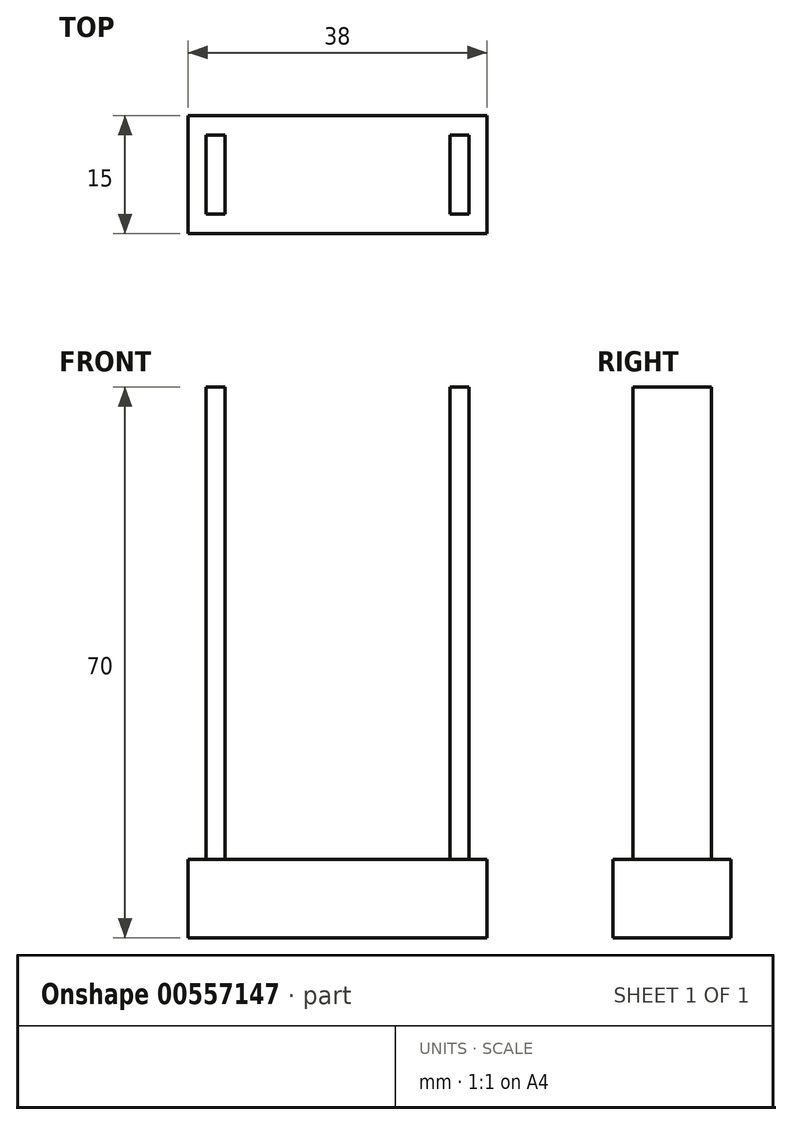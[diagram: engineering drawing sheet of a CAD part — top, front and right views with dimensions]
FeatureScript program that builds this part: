
annotation { "Feature Type Name" : "Feature", "Feature Type Description" : "" }
export const myFeature = defineFeature(function(context is Context, id is Id, definition is map)
    precondition{}
    {
        {
            var Q0;
            Q0=qCreatedBy(makeId("Top.planeOp"),FACE);
            var sketch = newSketch(context, id + "F0", { "sketchPlane" : qUnion([Q0])});
            skLineSegment(sketch, "E0", {"start": v(0, 0) * mm, "end": v(15.5, 0) * mm});
            skLineSegment(sketch, "E1", {"start": v(15.5, 0) * mm, "end": v(-15.5, 0) * mm});
            skLineSegment(sketch, "E2", {"start": v(-15.5, 0) * mm, "end": v(-14.3, 0) * mm});
            skLineSegment(sketch, "E3", {"start": v(-14.3, 0) * mm, "end": v(-14.3, 5) * mm});
            skLineSegment(sketch, "E4", {"start": v(-14.3, 5) * mm, "end": v(-14.3, -5) * mm});
            skLineSegment(sketch, "E5", {"start": v(-14.3, -5) * mm, "end": v(-16.7, -5) * mm});
            skLineSegment(sketch, "E6.bottom", {"start": v(-16.7, -5) * mm, "end": v(-14.3, -5) * mm});
            skLineSegment(sketch, "E6.top", {"start": v(-16.7, 5) * mm, "end": v(-14.3, 5) * mm});
            skLineSegment(sketch, "E6.left", {"start": v(-16.7, -5) * mm, "end": v(-16.7, 5) * mm});
            skLineSegment(sketch, "E6.right", {"start": v(-14.3, -5) * mm, "end": v(-14.3, 5) * mm});
            skLineSegment(sketch, "E7", {"start": v(15.5, 0) * mm, "end": v(14.3, 0) * mm});
            skLineSegment(sketch, "E8", {"start": v(14.3, 0) * mm, "end": v(14.3, 5) * mm});
            skLineSegment(sketch, "E9", {"start": v(14.3, 5) * mm, "end": v(14.3, -5) * mm});
            skLineSegment(sketch, "E10", {"start": v(14.3, -5) * mm, "end": v(16.7, -5) * mm});
            skLineSegment(sketch, "E11.bottom", {"start": v(14.3, 5) * mm, "end": v(16.7, 5) * mm});
            skLineSegment(sketch, "E11.right", {"start": v(16.7, 5) * mm, "end": v(16.7, -5) * mm});
            skSolve(sketch);
        }
        {
            var Q0;
            Q0=qCreatedBy(makeId("Top.planeOp"),FACE);
            var sketch = newSketch(context, id + "F1", { "sketchPlane" : qUnion([Q0])});
            skLineSegment(sketch, "E12.bottom", {"start": v(19, 7.5) * mm, "end": v(-19, 7.5) * mm});
            skLineSegment(sketch, "E12.top", {"start": v(19, -7.5) * mm, "end": v(-19, -7.5) * mm});
            skLineSegment(sketch, "E12.left", {"start": v(19, 7.5) * mm, "end": v(19, -7.5) * mm});
            skLineSegment(sketch, "E12.right", {"start": v(-19, 7.5) * mm, "end": v(-19, -7.5) * mm});
            skPoint(sketch, "E12.middle", {"position": v(0, 0) * mm});
            skSolve(sketch);
        }
        {
            var Q0;
            Q0 = qSketchRegion(id + "F0", true);
            extrude(context, id + "F2", {"entities" : qUnion([Q0]), "depth" : 60 * mm, "offsetDistance" : 25 * mm});
        }
        {
            var Q0;
            Q0=makeQuery(id+"F1.imprint","IMPRINT",FACE,{"disambiguationData":[TD([[makeQuery(id+"F1.imprint","IMPRINT",EDGE,{"derivedFrom":sQuery(id+"F1.wireOp",EDGE,"E12.bottom")}),1.0]])]});
            extrude(context, id + "F3", {"entities" : qUnion([Q0]), "oppositeDirection" : true, "depth" : 10 * mm, "offsetDistance" : 25 * mm});
        }
    });
